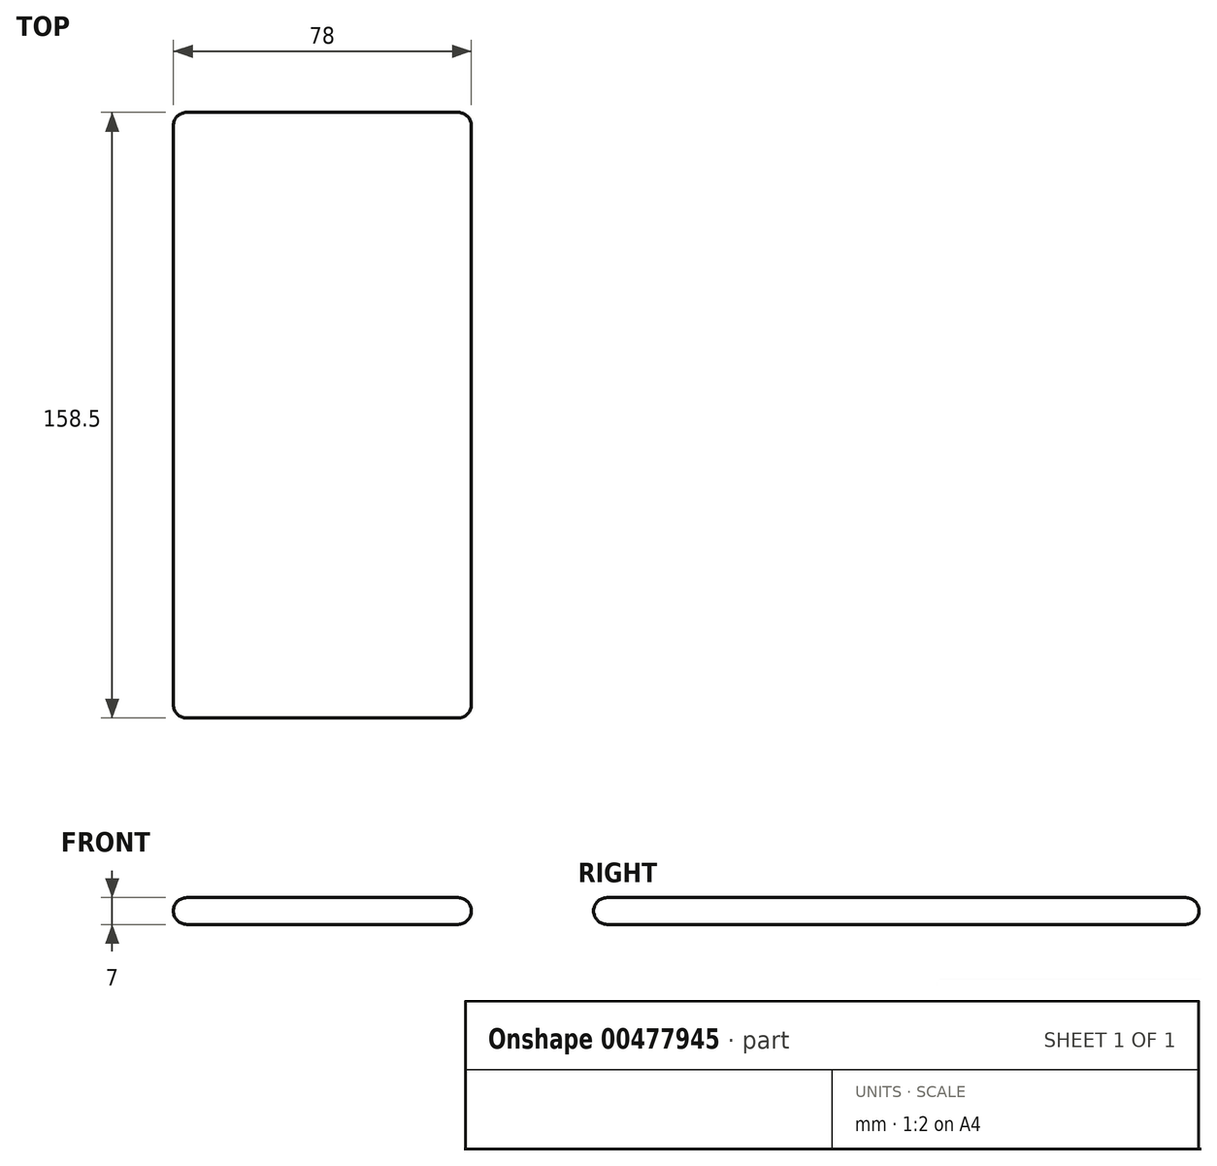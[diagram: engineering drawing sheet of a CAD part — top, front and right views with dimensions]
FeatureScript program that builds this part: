
annotation { "Feature Type Name" : "Feature", "Feature Type Description" : "" }
export const myFeature = defineFeature(function(context is Context, id is Id, definition is map)
    precondition{}
    {
        {
            var Q0;
            Q0=qCreatedBy(makeId("Top.planeOp"),FACE);
            var sketch = newSketch(context, id + "F0", { "sketchPlane" : qUnion([Q0])});
            skLineSegment(sketch, "E0.bottom", {"start": v(-39, 79.25) * mm, "end": v(39, 79.25) * mm});
            skLineSegment(sketch, "E0.top", {"start": v(-39, -79.25) * mm, "end": v(39, -79.25) * mm});
            skLineSegment(sketch, "E0.left", {"start": v(-39, 79.25) * mm, "end": v(-39, -79.25) * mm});
            skLineSegment(sketch, "E0.right", {"start": v(39, 79.25) * mm, "end": v(39, -79.25) * mm});
            skPoint(sketch, "E0.middle", {"position": v(0, 0) * mm});
            skCircle(sketch, "E1", {"center": v(0, -69.5) * mm, "radius": 5.75 * mm});
            skLineSegment(sketch, "E2.bottom", {"start": v(-7, 69.25) * mm, "end": v(7, 69.25) * mm});
            skLineSegment(sketch, "E2.top", {"start": v(-7, 70.25) * mm, "end": v(7, 70.25) * mm});
            skLineSegment(sketch, "E2.left", {"start": v(-7, 69.25) * mm, "end": v(-7, 70.25) * mm});
            skLineSegment(sketch, "E2.right", {"start": v(7, 69.25) * mm, "end": v(7, 70.25) * mm});
            skPoint(sketch, "E2.middle", {"position": v(0, 69.75) * mm});
            skLineSegment(sketch, "E3.bottom", {"start": v(11.5, 73.75) * mm, "end": v(33.5, 73.75) * mm});
            skLineSegment(sketch, "E3.top", {"start": v(11.5, 61.75) * mm, "end": v(33.5, 61.75) * mm});
            skLineSegment(sketch, "E3.left", {"start": v(11.5, 73.75) * mm, "end": v(11.5, 61.75) * mm});
            skLineSegment(sketch, "E3.right", {"start": v(33.5, 73.75) * mm, "end": v(33.5, 61.75) * mm});
            skPoint(sketch, "E3.middle", {"position": v(22.5, 67.75) * mm});
            skCircle(sketch, "E4", {"center": v(26.47, 67.75) * mm, "radius": 3.08 * mm, "construction": true});
            skCircle(sketch, "E5", {"center": v(18.72, 67.75) * mm, "radius": 2.2 * mm, "construction": true});
            skCircle(sketch, "E6", {"center": v(7.56, 67.75) * mm, "radius": 1.32 * mm, "construction": true});
            skCircle(sketch, "E7", {"center": v(2.08, 67.75) * mm, "radius": 2.57 * mm, "construction": true});
            skCircle(sketch, "E8", {"center": v(-13.75, 69.75) * mm, "radius": 0.75 * mm});
            skSolve(sketch);
        }
        {
            var Q0;
            Q0=makeQuery(id+"F0.imprint","IMPRINT",FACE,{"disambiguationData":[TD([[makeQuery(id+"F0.imprint","IMPRINT",EDGE,{"derivedFrom":sQuery(id+"F0.wireOp",EDGE,"E0.bottom")}),-1.0]])]});
            var Q1;
            Q1=makeQuery(id+"F0.imprint","IMPRINT",FACE,{"disambiguationData":[TD([[makeQuery(id+"F0.imprint","IMPRINT",EDGE,{"derivedFrom":sQuery(id+"F0.wireOp",EDGE,"E1")}),1.0]])]});
            var Q2;
            Q2=makeQuery(id+"F0.imprint","IMPRINT",FACE,{"disambiguationData":[TD([[makeQuery(id+"F0.imprint","IMPRINT",EDGE,{"derivedFrom":sQuery(id+"F0.wireOp",EDGE,"E3.bottom")}),-1.0]])]});
            var Q3;
            Q3=makeQuery(id+"F0.imprint","IMPRINT",FACE,{"disambiguationData":[TD([[makeQuery(id+"F0.imprint","IMPRINT",EDGE,{"derivedFrom":sQuery(id+"F0.wireOp",EDGE,"E2.bottom")}),1.0]])]});
            var Q4;
            Q4=makeQuery(id+"F0.imprint","IMPRINT",FACE,{"disambiguationData":[TD([[makeQuery(id+"F0.imprint","IMPRINT",EDGE,{"derivedFrom":sQuery(id+"F0.wireOp",EDGE,"E8")}),1.0]])]});
            extrude(context, id + "F1", {"entities" : qUnion([Q0, Q1, Q2, Q3, Q4]), "depth" : 7 * mm, "offsetDistance" : 25 * mm});
        }
        {
            var Q0;
            Q0=makeQuery(id+"F1.opExtrude","CAP_EDGE",EDGE,{"disambiguationData":[OSD([sQuery(id+"F0.wireOp",EDGE,"E0.right")])],"isStart":false});
            var Q1;
            Q1=makeQuery(id+"F1.opExtrude","CAP_EDGE",EDGE,{"disambiguationData":[OSD([sQuery(id+"F0.wireOp",EDGE,"E0.left")])],"isStart":false});
            var Q2;
            Q2=makeQuery(id+"F1.opExtrude","CAP_EDGE",EDGE,{"disambiguationData":[OSD([sQuery(id+"F0.wireOp",EDGE,"E0.top")])],"isStart":false});
            var Q3;
            Q3=makeQuery(id+"F1.opExtrude","CAP_EDGE",EDGE,{"disambiguationData":[OSD([sQuery(id+"F0.wireOp",EDGE,"E0.bottom")])],"isStart":false});
            var Q4;
            Q4=makeQuery(id+"F1.opExtrude","CAP_EDGE",EDGE,{"disambiguationData":[OSD([sQuery(id+"F0.wireOp",EDGE,"E0.right")])],"isStart":true});
            var Q5;
            Q5=makeQuery(id+"F1.opExtrude","CAP_EDGE",EDGE,{"disambiguationData":[OSD([sQuery(id+"F0.wireOp",EDGE,"E0.top")])],"isStart":true});
            var Q6;
            Q6=makeQuery(id+"F1.opExtrude","CAP_EDGE",EDGE,{"disambiguationData":[OSD([sQuery(id+"F0.wireOp",EDGE,"E0.bottom")])],"isStart":true});
            var Q7;
            Q7=makeQuery(id+"F1.opExtrude","CAP_EDGE",EDGE,{"disambiguationData":[OSD([sQuery(id+"F0.wireOp",EDGE,"E0.left")])],"isStart":true});
            var Q8;
            Q8=makeQuery(id+"F1.opExtrude","SWEPT_EDGE",EDGE,{"disambiguationData":[OSD([sQuery(id+"F0.wireOp",EDGE,"E0.bottom"),sQuery(id+"F0.wireOp",EDGE,"E0.left")])]});
            var Q9;
            Q9=makeQuery(id+"F1.opExtrude","SWEPT_EDGE",EDGE,{"disambiguationData":[OSD([sQuery(id+"F0.wireOp",EDGE,"E0.bottom"),sQuery(id+"F0.wireOp",EDGE,"E0.right")])]});
            var Q10;
            Q10=makeQuery(id+"F1.opExtrude","SWEPT_EDGE",EDGE,{"disambiguationData":[OSD([sQuery(id+"F0.wireOp",EDGE,"E0.top"),sQuery(id+"F0.wireOp",EDGE,"E0.left")])]});
            var Q11;
            Q11=makeQuery(id+"F1.opExtrude","SWEPT_EDGE",EDGE,{"disambiguationData":[OSD([sQuery(id+"F0.wireOp",EDGE,"E0.top"),sQuery(id+"F0.wireOp",EDGE,"E0.right")])]});
            fillet(context, id + "F2", {"entities" : qUnion([Q0, Q1, Q2, Q3, Q4, Q5, Q6, Q7, Q8, Q9, Q10, Q11]), "radius" : 3.5 * mm, "tangentPropagation" : true, "allowEdgeOverflow" : false});
        }
    });
